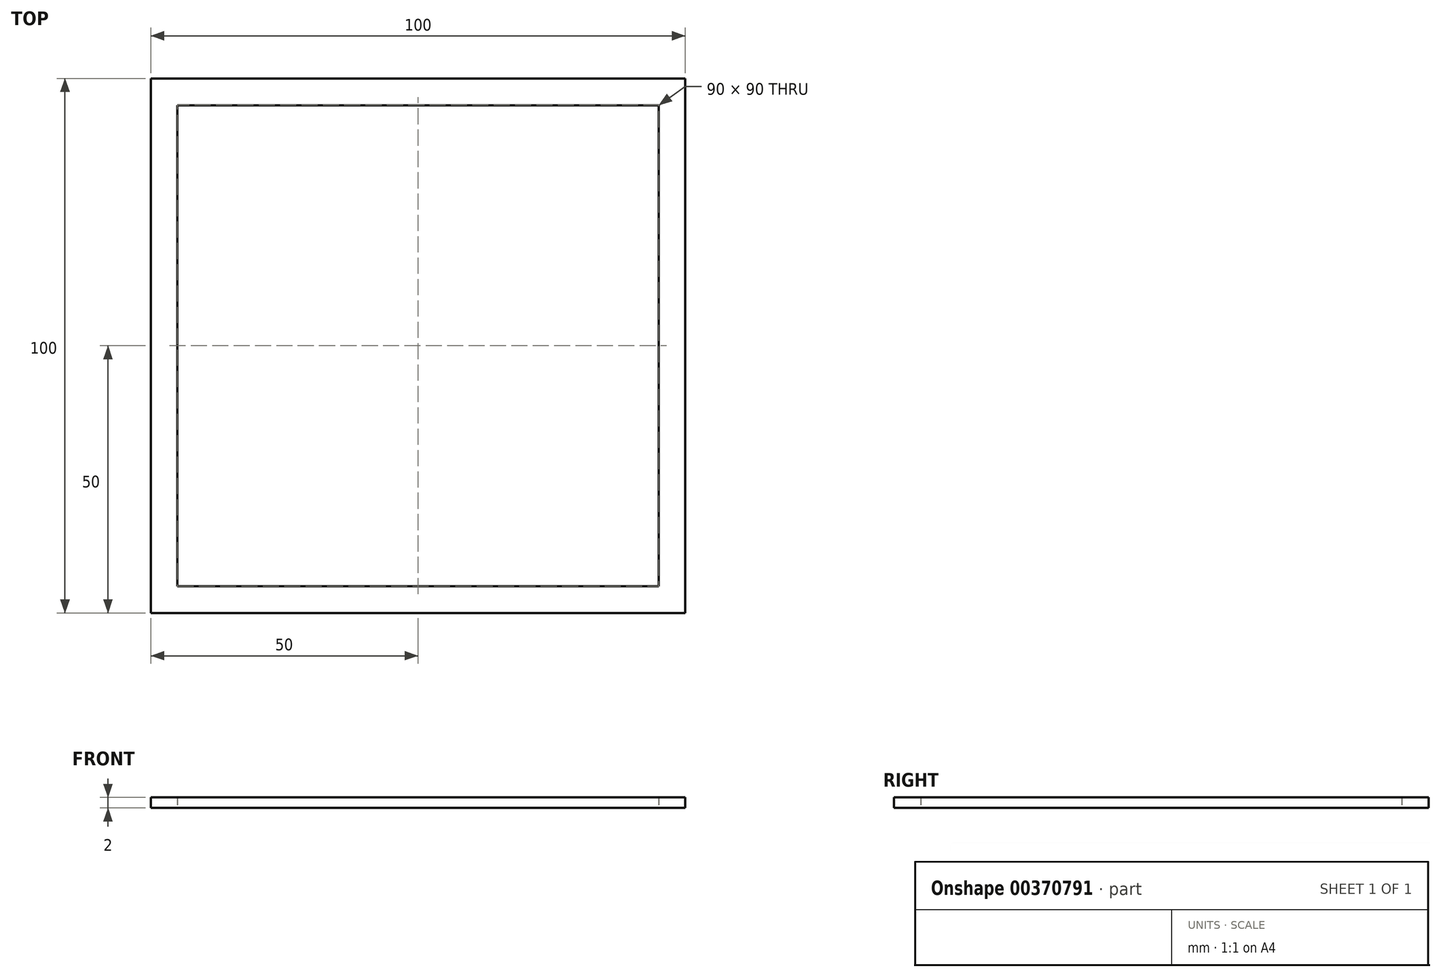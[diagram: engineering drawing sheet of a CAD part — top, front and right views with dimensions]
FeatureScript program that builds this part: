
annotation { "Feature Type Name" : "Feature", "Feature Type Description" : "" }
export const myFeature = defineFeature(function(context is Context, id is Id, definition is map)
    precondition{}
    {
        {
            var Q0;
            Q0=qCreatedBy(makeId("Top.planeOp"),FACE);
            var sketch = newSketch(context, id + "F0", { "sketchPlane" : qUnion([Q0])});
            skLineSegment(sketch, "E0.bottom", {"start": v(50, 50) * mm, "end": v(-50, 50) * mm});
            skLineSegment(sketch, "E0.top", {"start": v(50, -50) * mm, "end": v(-50, -50) * mm});
            skLineSegment(sketch, "E0.left", {"start": v(50, 50) * mm, "end": v(50, -50) * mm});
            skLineSegment(sketch, "E0.right", {"start": v(-50, 50) * mm, "end": v(-50, -50) * mm});
            skPoint(sketch, "E0.middle", {"position": v(0, 0) * mm});
            skLineSegment(sketch, "E1.bottom", {"start": v(45, 45) * mm, "end": v(-45, 45) * mm});
            skLineSegment(sketch, "E1.top", {"start": v(45, -45) * mm, "end": v(-45, -45) * mm});
            skLineSegment(sketch, "E1.left", {"start": v(45, 45) * mm, "end": v(45, -45) * mm});
            skLineSegment(sketch, "E1.right", {"start": v(-45, 45) * mm, "end": v(-45, -45) * mm});
            skSolve(sketch);
        }
        {
            var Q0;
            Q0=makeQuery(id+"F0.imprint","IMPRINT",FACE,{"disambiguationData":[TD([[makeQuery(id+"F0.imprint","IMPRINT",EDGE,{"derivedFrom":sQuery(id+"F0.wireOp",EDGE,"E0.bottom")}),1.0]])]});
            extrude(context, id + "F1", {"entities" : qUnion([Q0]), "depth" : 2 * mm});
        }
    });
